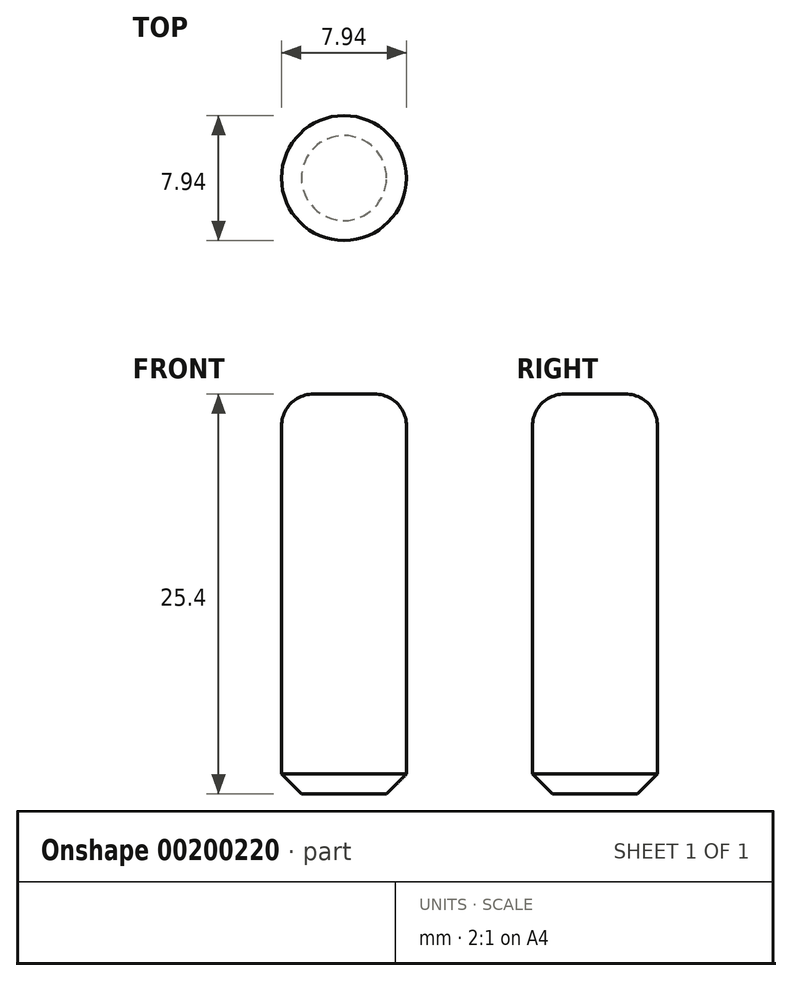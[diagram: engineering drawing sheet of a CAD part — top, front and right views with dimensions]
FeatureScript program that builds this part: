
annotation { "Feature Type Name" : "Feature", "Feature Type Description" : "" }
export const myFeature = defineFeature(function(context is Context, id is Id, definition is map)
    precondition{}
    {
        {
            var Q0;
            Q0=qCreatedBy(makeId("Top.planeOp"),FACE);
            var sketch = newSketch(context, id + "F0", { "sketchPlane" : qUnion([Q0])});
            skCircle(sketch, "E0", {"center": v(0, 0) * mm, "radius": 3.97 * mm});
            skSolve(sketch);
        }
        {
            var Q0;
            Q0 = qSketchRegion(id + "F0", true);
            extrude(context, id + "F1", {"entities" : qUnion([Q0]), "depth" : 25.4 * mm});
        }
        {
            var Q0;
            Q0=makeQuery(id+"F1.opExtrude","CAP_EDGE",EDGE,{"disambiguationData":[OSD([sQuery(id+"F0.wireOp",EDGE,"E0")])],"isStart":true});
            chamfer(context, id + "F2", {"entities" : qUnion([Q0]), "width" : 1.27 * mm, "tangentPropagation" : true});
        }
        {
            var Q0;
            Q0=makeQuery(id+"F1.opExtrude","CAP_EDGE",EDGE,{"disambiguationData":[OSD([sQuery(id+"F0.wireOp",EDGE,"E0")])],"isStart":false});
            fillet(context, id + "F3", {"entities" : qUnion([Q0]), "radius" : 2.03 * mm, "tangentPropagation" : true, "allowEdgeOverflow" : false});
        }
    });
